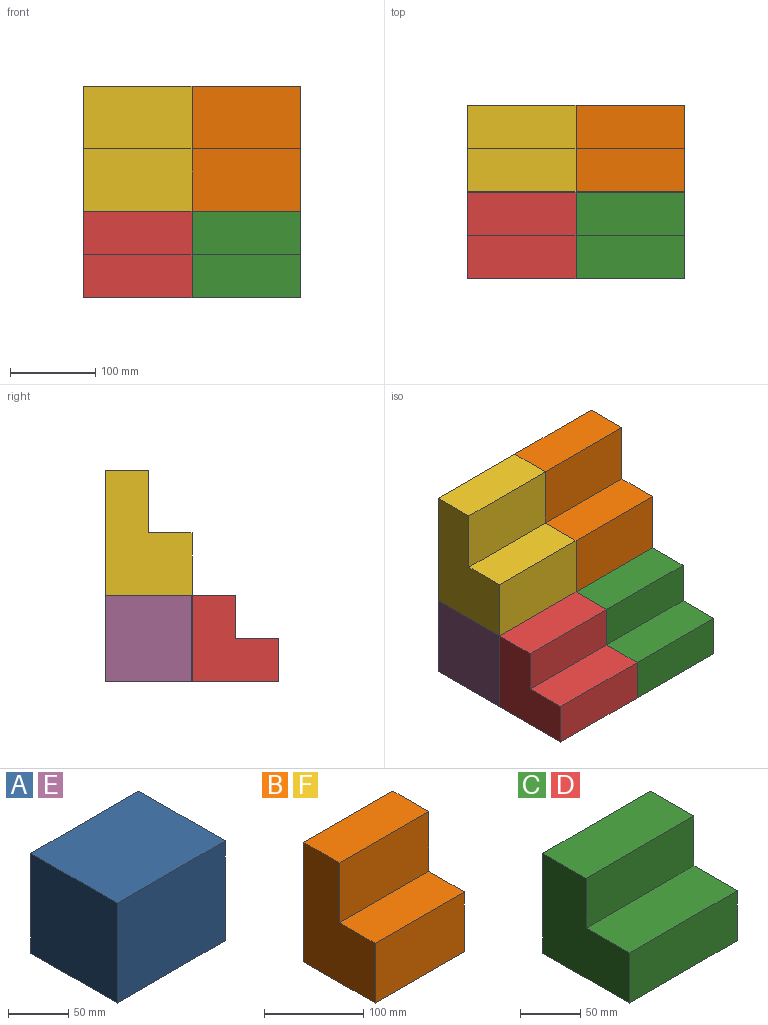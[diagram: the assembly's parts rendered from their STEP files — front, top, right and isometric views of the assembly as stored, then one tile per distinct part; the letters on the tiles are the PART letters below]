
ASSEMBLY  parts=6 mates=11
PART A: 6 faces, bbox 127x101.6x101.6 mm
  f0: plane 127x101.6mm, normal (0,0,1), area 12903.2mm2, adj f1,f3,f4,f5
  f1: plane 127x101.6mm, normal (0,-1,0), area 12903.2mm2, adj f0,f2,f4,f5
  f2: plane 127x101.6mm, normal (0,0,-1), area 12903.2mm2, adj f1,f3,f4,f5
  f3: plane 127x101.6mm, normal (0,1,0), area 12903.2mm2, adj f0,f2,f4,f5
  f4: plane 101.6x101.6mm, normal (1,0,0), area 10322.6mm2, adj f0,f1,f2,f3
  f5: plane 101.6x101.6mm, normal (-1,0,0), area 10322.6mm2, adj f0,f1,f2,f3
PART B: 8 faces, bbox 127x101.6x147.3 mm
  f0: plane 127x73.66mm, normal (0,-1,0), area 9354.8mm2, adj f1,f5,f6,f7
  f1: plane 127x101.6mm, normal (0,0,-1), area 12903.2mm2, adj f0,f2,f6,f7
  f2: plane 147.32x127mm, normal (0,1,0), area 18709.6mm2, adj f1,f3,f6,f7
  f3: plane 127x50.8mm, normal (0,0,1), area 6451.6mm2, adj f2,f4,f6,f7
  f4: plane 127x73.66mm, normal (0,-1,0), area 9354.8mm2, adj f3,f5,f6,f7
  f5: plane 127x50.8mm, normal (0,0,1), area 6451.6mm2, adj f0,f4,f6,f7
  f6: plane 147.32x101.6mm, normal (1,0,0), area 11225.8mm2, adj f0,f1,f2,f3,f4,f5
  f7: plane 147.32x101.6mm, normal (-1,0,0), area 11225.8mm2, adj f0,f1,f2,f3,f4,f5
PART C: 8 faces, bbox 127x101.6x101.6 mm
  f0: plane 127x50.8mm, normal (0,-1,0), area 6451.6mm2, adj f1,f5,f6,f7
  f1: plane 127x101.6mm, normal (0,0,-1), area 12903.2mm2, adj f0,f2,f6,f7
  f2: plane 127x101.6mm, normal (0,1,0), area 12903.2mm2, adj f1,f3,f6,f7
  f3: plane 127x50.8mm, normal (0,0,1), area 6451.6mm2, adj f2,f4,f6,f7
  f4: plane 127x50.8mm, normal (0,-1,0), area 6451.6mm2, adj f3,f5,f6,f7
  f5: plane 127x50.8mm, normal (0,0,1), area 6451.6mm2, adj f0,f4,f6,f7
  f6: plane 101.6x101.6mm, normal (1,0,0), area 7741.9mm2, adj f0,f1,f2,f3,f4,f5
  f7: plane 101.6x101.6mm, normal (-1,0,0), area 7741.9mm2, adj f0,f1,f2,f3,f4,f5
PART D: same geometry as C
PART E: same geometry as A
PART F: same geometry as B
PLACE A t=(127,101.6,0)mm
PLACE B t=(127,101.6,101.6)mm
PLACE C t=(127,0,0)mm
PLACE D at identity
PLACE E t=(0,101.6,0)mm
PLACE F t=(0,101.6,101.6)mm
MATE planar A.f1 <-> C.f2  axis (0,-1,0) through (190.5,101.6,50.8)mm
MATE planar F.f7 <-> E.f5  axis (-1,0,0) through (0,160.87,162.98)mm
MATE planar E.f1 <-> D.f2  axis (0,-1,0) through (63.5,101.6,50.8)mm
MATE planar A.f0 <-> B.f1  axis (0,0,1) through (190.5,152.4,101.6)mm
MATE planar F.f1 <-> E.f0  axis (0,0,-1) through (63.5,152.4,101.6)mm
MATE planar E.f5 <-> D.f7  axis (-1,0,0) through (0,152.4,50.8)mm
MATE planar A.f2 <-> C.f1  axis (0,0,-1) through (190.5,152.4,0)mm
MATE planar A.f3 <-> B.f2  axis (0,1,0) through (190.5,203.2,50.8)mm
MATE planar B.f6 <-> A.f4  axis (1,0,0) through (254,160.87,162.98)mm
MATE planar C.f7 <-> D.f6  axis (-1,0,0) through (127,59.27,42.33)mm
MATE planar E.f2 <-> D.f1  axis (0,0,-1) through (63.5,152.4,0)mm
